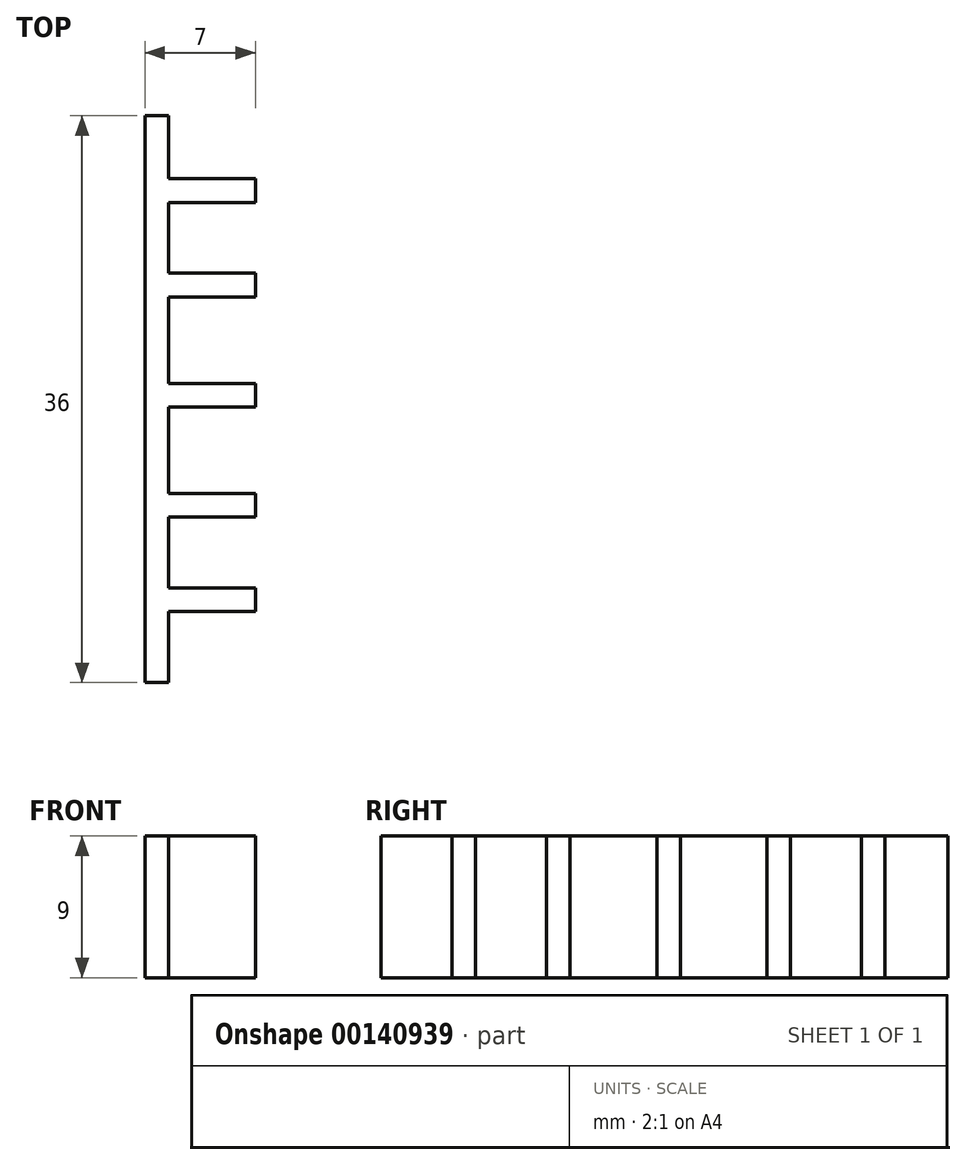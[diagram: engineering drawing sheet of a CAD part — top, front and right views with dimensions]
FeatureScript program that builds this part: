
annotation { "Feature Type Name" : "Feature", "Feature Type Description" : "" }
export const myFeature = defineFeature(function(context is Context, id is Id, definition is map)
    precondition{}
    {
        {
            var Q0;
            Q0=qCreatedBy(makeId("Top.planeOp"),FACE);
            var sketch = newSketch(context, id + "F0", { "sketchPlane" : qUnion([Q0])});
            skLineSegment(sketch, "E0", {"start": v(0, 0) * mm, "end": v(0, -36) * mm});
            skLineSegment(sketch, "E1", {"start": v(0, -36) * mm, "end": v(1.5, -36) * mm});
            skLineSegment(sketch, "E2", {"start": v(1.5, 0) * mm, "end": v(0, 0) * mm});
            skLineSegment(sketch, "E3", {"start": v(1.5, 0) * mm, "end": v(1.5, -36) * mm, "construction": true});
            skLineSegment(sketch, "E4", {"start": v(7, 0) * mm, "end": v(7, -36.14) * mm, "construction": true});
            skLineSegment(sketch, "E5", {"start": v(1.5, -36) * mm, "end": v(1.5, -31.5) * mm});
            skLineSegment(sketch, "E6", {"start": v(1.5, -31.5) * mm, "end": v(7, -31.5) * mm});
            skLineSegment(sketch, "E7", {"start": v(7, -31.5) * mm, "end": v(7, -30) * mm});
            skLineSegment(sketch, "E8", {"start": v(7, -30) * mm, "end": v(1.5, -30) * mm});
            skLineSegment(sketch, "E9", {"start": v(1.5, -30) * mm, "end": v(1.5, -25.5) * mm});
            skLineSegment(sketch, "E10", {"start": v(1.5, -25.5) * mm, "end": v(7, -25.5) * mm});
            skLineSegment(sketch, "E11", {"start": v(7, -25.5) * mm, "end": v(7, -24) * mm});
            skLineSegment(sketch, "E12", {"start": v(7, -24) * mm, "end": v(1.5, -24) * mm});
            skLineSegment(sketch, "E13", {"start": v(1.5, -24) * mm, "end": v(1.5, -18.5) * mm});
            skLineSegment(sketch, "E14", {"start": v(1.5, -18.5) * mm, "end": v(7, -18.5) * mm});
            skLineSegment(sketch, "E15", {"start": v(7, -18.5) * mm, "end": v(7, -17) * mm});
            skLineSegment(sketch, "E16", {"start": v(7, -17) * mm, "end": v(1.5, -17) * mm});
            skLineSegment(sketch, "E17", {"start": v(1.5, -17) * mm, "end": v(1.5, -11.5) * mm});
            skLineSegment(sketch, "E18", {"start": v(1.5, -11.5) * mm, "end": v(7, -11.5) * mm});
            skLineSegment(sketch, "E19", {"start": v(7, -11.5) * mm, "end": v(7, -10) * mm});
            skLineSegment(sketch, "E20", {"start": v(7, -10) * mm, "end": v(1.5, -10) * mm});
            skLineSegment(sketch, "E21", {"start": v(1.5, -10) * mm, "end": v(1.5, -5.5) * mm});
            skLineSegment(sketch, "E22", {"start": v(1.5, -5.5) * mm, "end": v(7, -5.5) * mm});
            skLineSegment(sketch, "E23", {"start": v(7, -5.5) * mm, "end": v(7, -4) * mm});
            skLineSegment(sketch, "E24", {"start": v(7, -4) * mm, "end": v(1.5, -4) * mm});
            skLineSegment(sketch, "E25", {"start": v(1.5, -4) * mm, "end": v(1.5, 0) * mm});
            skSolve(sketch);
        }
        {
            var Q0;
            Q0=makeQuery(id+"F0.imprint","IMPRINT",FACE,{"disambiguationData":[TD([[makeQuery(id+"F0.imprint","IMPRINT",EDGE,{"derivedFrom":sQuery(id+"F0.wireOp",EDGE,"E0")}),1.0]])]});
            extrude(context, id + "F1", {"entities" : qUnion([Q0]), "depth" : 9 * mm});
        }
    });
